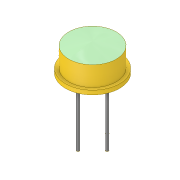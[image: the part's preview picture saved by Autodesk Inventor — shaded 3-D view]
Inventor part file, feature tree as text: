
AUTODESK INVENTOR PART (.ipt)
format: ipt  version: 2017 (Build 210142000, 142)  size: 186,368 bytes
history: native  units: in
note: dims shown in document units (in); Inventor stores cm internally (conversion verified against a paired STEP export)
features: sketch x5, extrude x3, revolve x2, fillet x1
ambient origin geometry x8: Origin, YZ Plane, XZ Plane, XY Plane, X Axis, Y Axis, Z Axis, Center Point
bodies: Solid1 (feature_tree)
feature tree (11):
  revolve  "Revolution1"  [1 undecoded]
  revolve  "Revolution2"  [1 undecoded]
  extrude  "Extrusion1"  TaperAngle=90.0deg  [1 undecoded]
  fillet  "Fillet1"  [1 undecoded]
  extrude  "Extrusion2"  Depth=0.031in
  extrude  "Extrusion3"  Depth=0.0075in
  sketch  "Sketch1"  dims[d0=0.028in d1=0.15in]
  sketch  "Sketch2"  dims[d2=0.185in d3=0.1625in]
  sketch  "Sketch3"  dims[d4=0.163in d5=90.0deg d6=90.0deg]
  sketch  "Sketch4"  dims[d7=0.031in d8=0.035in]
  sketch  "Sketch5"  dims[d9=1.0in d10=0.0in d11=0.0075in d12=0.019in d13=0.1in d14=1.5748in d16=360.0deg d18=1.0in d19=0.0in d20=1.0in d21=0.0in]
note: 4 required parameter values undecoded (feature->parameter linkage not recoverable at this tier; creation-order binding heuristic only, values carry confidence <= 0.55)